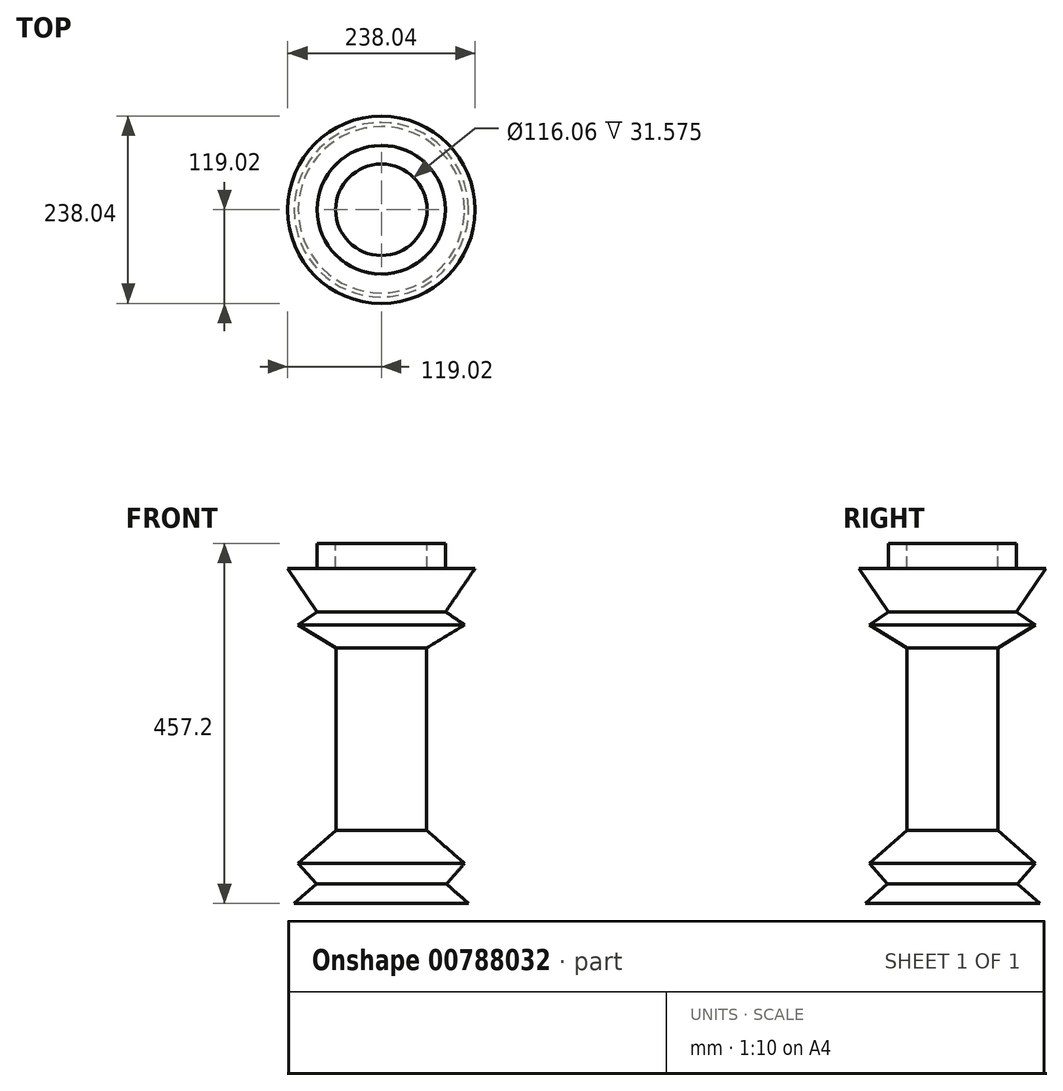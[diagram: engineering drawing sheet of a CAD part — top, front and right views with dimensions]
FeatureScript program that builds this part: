
annotation { "Feature Type Name" : "Feature", "Feature Type Description" : "" }
export const myFeature = defineFeature(function(context is Context, id is Id, definition is map)
    precondition{}
    {
        {
            var Q0;
            Q0=qCreatedBy(makeId("Front.planeOp"),FACE);
            var sketch = newSketch(context, id + "F0", { "sketchPlane" : qUnion([Q0])});
            skLineSegment(sketch, "E0", {"start": v(0, 339.38) * mm, "end": v(0, -342.9) * mm});
            skLineSegment(sketch, "E1", {"start": v(0, -342.9) * mm, "end": v(-110.78, -342.9) * mm});
            skLineSegment(sketch, "E2", {"start": v(-110.78, -342.9) * mm, "end": v(-82.65, -318.28) * mm});
            skLineSegment(sketch, "E3", {"start": v(-82.65, -318.28) * mm, "end": v(-105.6, -292.06) * mm});
            skLineSegment(sketch, "E4", {"start": v(-105.6, -292.06) * mm, "end": v(-57.54, -250) * mm});
            skLineSegment(sketch, "E5", {"start": v(-57.54, -250) * mm, "end": v(-57.54, -18.17) * mm});
            skLineSegment(sketch, "E6", {"start": v(-57.54, -18.17) * mm, "end": v(-105.6, 11.14) * mm});
            skLineSegment(sketch, "E7", {"start": v(-105.6, 11.14) * mm, "end": v(-81.48, 27.55) * mm});
            skLineSegment(sketch, "E8", {"start": v(-81.48, 27.55) * mm, "end": v(-119.02, 82.72) * mm});
            skLineSegment(sketch, "E9", {"start": v(-119.02, 82.72) * mm, "end": v(0, 82.72) * mm});
            skLineSegment(sketch, "E10", {"start": v(-81.57, 82.72) * mm, "end": v(-81.57, 114.3) * mm});
            skPoint(sketch, "E10.startSnap0", {"position": v(-81.57, -3.52) * mm});
            skLineSegment(sketch, "E11", {"start": v(-81.57, 114.3) * mm, "end": v(-58.03, 114.3) * mm});
            skLineSegment(sketch, "E12", {"start": v(-58.03, 114.3) * mm, "end": v(-58.03, 82.72) * mm});
            skSolve(sketch);
        }
        {
            var Q0;
            Q0 = qSketchRegion(id + "F0", true);
            var Q1;
            Q1=sQuery(id+"F0.wireOp",EDGE,"E0");
            revolve(context, id + "F1", {"surfaceOperationType" : NewSurfaceOperationType.NEW, "entities" : qUnion([Q0]), "axis" : qUnion([Q1]), "revolveType" : RevolveType.FULL});
        }
    });
